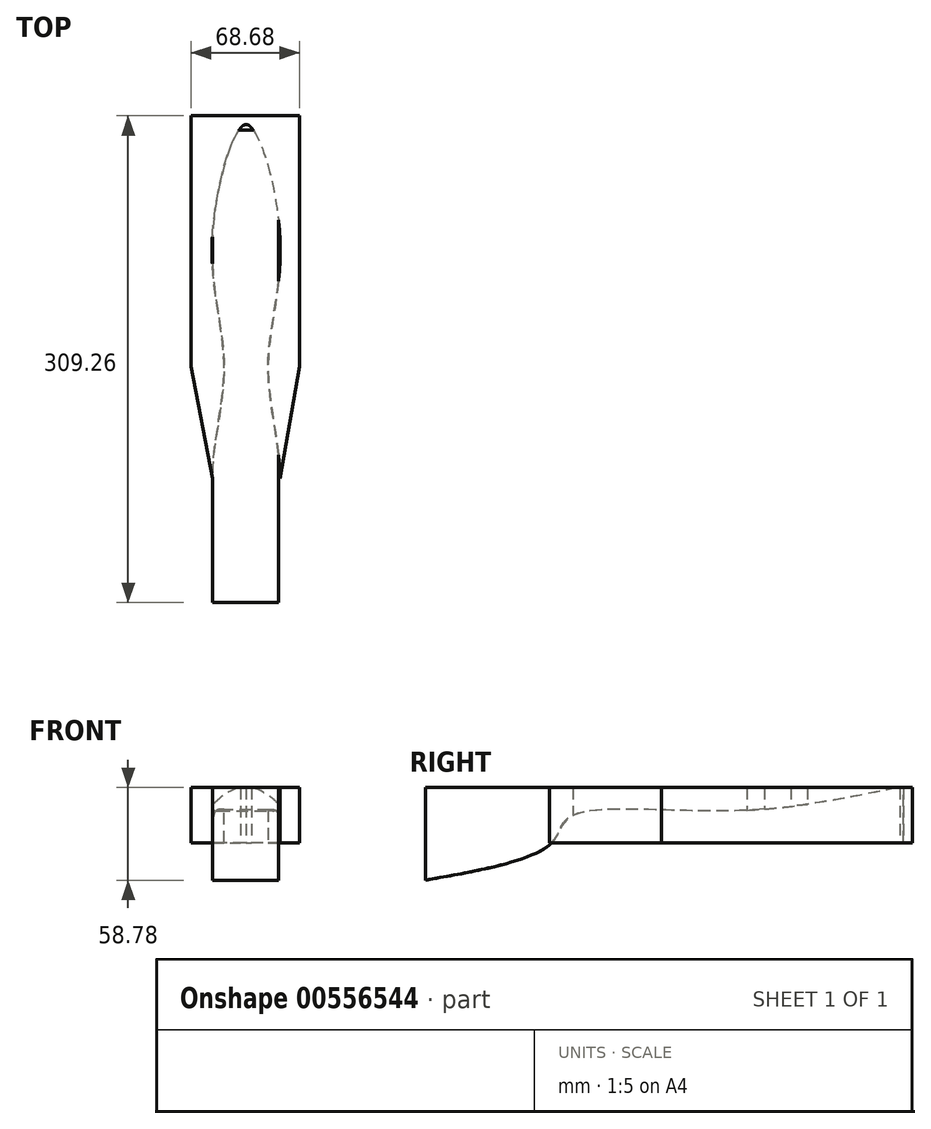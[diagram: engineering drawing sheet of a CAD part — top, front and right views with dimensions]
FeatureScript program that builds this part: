
annotation { "Feature Type Name" : "Feature", "Feature Type Description" : "" }
export const myFeature = defineFeature(function(context is Context, id is Id, definition is map)
    precondition{}
    {
        {
            var Q0;
            Q0=qCreatedBy(makeId("Top.planeOp"),FACE);
            var sketch = newSketch(context, id + "F0", { "sketchPlane" : qUnion([Q0])});
            skFitSpline(sketch, "E0", {"points": [v(0, -71.02) * mm, v(7.48, 0) * mm, v(0, 82.23) * mm, v(21.44, 153.63) * mm, v(40.93, 82.42) * mm], "startDerivative": vector(0, 283.1) * mm, "endDerivative": vector(68.58, -404.85) * mm});
            skLineSegment(sketch, "E1", {"start": v(21.44, 153.63) * mm, "end": v(21.44, 0) * mm});
            skPoint(sketch, "E2.1.internal.orphan", {"position": v(34.16, 0) * mm});
            skFitSpline(sketch, "E3.MirrorCS", {"points": [v(42.88, -71.02) * mm, v(35.4, 0) * mm, v(42.88, 82.23) * mm, v(21.44, 153.63) * mm, v(1.95, 82.42) * mm], "startDerivative": vector(0, 283.1) * mm, "endDerivative": vector(-68.58, -404.85) * mm});
            skLineSegment(sketch, "E4", {"start": v(42.88, -71.02) * mm, "end": v(55.26, 0) * mm});
            skLineSegment(sketch, "E5", {"start": v(55.26, 0) * mm, "end": v(55.26, 159.26) * mm});
            skLineSegment(sketch, "E6", {"start": v(55.26, 159.26) * mm, "end": v(-13.42, 159.26) * mm});
            skLineSegment(sketch, "E7", {"start": v(-13.42, 159.26) * mm, "end": v(-13.42, 0) * mm});
            skLineSegment(sketch, "E8", {"start": v(-13.42, 0) * mm, "end": v(0, -71.02) * mm});
            skSolve(sketch);
        }
        {
            var Q0;
            Q0=qCreatedBy(makeId("Right.planeOp"),FACE);
            var sketch = newSketch(context, id + "F1", { "sketchPlane" : qUnion([Q0])});
            skLineSegment(sketch, "E9.bottom", {"start": v(-150, 35) * mm, "end": v(150, 35) * mm});
            skLineSegment(sketch, "E9.left", {"start": v(-150, 35) * mm, "end": v(-150, -35) * mm});
            skPoint(sketch, "E9.middle", {"position": v(0, 0) * mm});
            skPoint(sketch, "E9.top.end.orphan", {"position": v(150, -35) * mm});
            skFitSpline(sketch, "E10", {"points": [v(-157.25, -25.02) * mm, v(-69.65, 0) * mm, v(-58.6, 16.22) * mm, v(38.91, 20.15) * mm, v(150, 35) * mm], "startDerivative": vector(411.57, 70.57) * mm, "endDerivative": vector(338.38, 69.9) * mm});
            skSolve(sketch);
        }
        {
            var Q0;
            Q0 = qSketchRegion(id + "F1", true);
            extrude(context, id + "F2", {"entities" : qUnion([Q0]), "depth" : 42 * mm, "offsetDistance" : 25 * mm});
        }
        {
            var Q0;
            Q0 = qSketchRegion(id + "F0", true);
            extrude(context, id + "F3", {"entities" : qUnion([Q0]), "operationType" : NewBodyOperationType.REMOVE, "oppositeDirection" : true, "depth" : 50 * mm, "offsetDistance" : 25 * mm});
        }
        {
            var Q0;
            Q0=makeQuery(id+"F0.imprint","IMPRINT",FACE,{"disambiguationData":[TD([[makeQuery(id+"F0.imprint","IMPRINT",EDGE,{"derivedFrom":sQuery(id+"F0.wireOp",EDGE,"E0")}),1.0]])]});
            var Q1;
            Q1=sQuery(id+"F0.wireOp",EDGE,"E7");
            var Q2;
            Q2=sQuery(id+"F0.wireOp",EDGE,"E8");
            var Q3;
            Q3=sQuery(id+"F0.wireOp",EDGE,"E0");
            var Q4;
            Q4=sQuery(id+"F0.wireOp",EDGE,"E3.MirrorCS");
            var Q5;
            Q5=sQuery(id+"F0.wireOp",EDGE,"E1");
            var Q6;
            Q6=sQuery(id+"F0.wireOp",EDGE,"E4");
            var Q7;
            Q7=sQuery(id+"F0.wireOp",EDGE,"E5");
            var Q8;
            Q8=sQuery(id+"F0.wireOp",EDGE,"E6");
            extrude(context, id + "F4", {"entities" : qUnion([Q0]), "operationType" : NewBodyOperationType.ADD, "surfaceEntities" : qUnion([Q1, Q2, Q3, Q4, Q5, Q6, Q7, Q8]), "depth" : 35 * mm, "offsetDistance" : 25 * mm});
        }
    });
